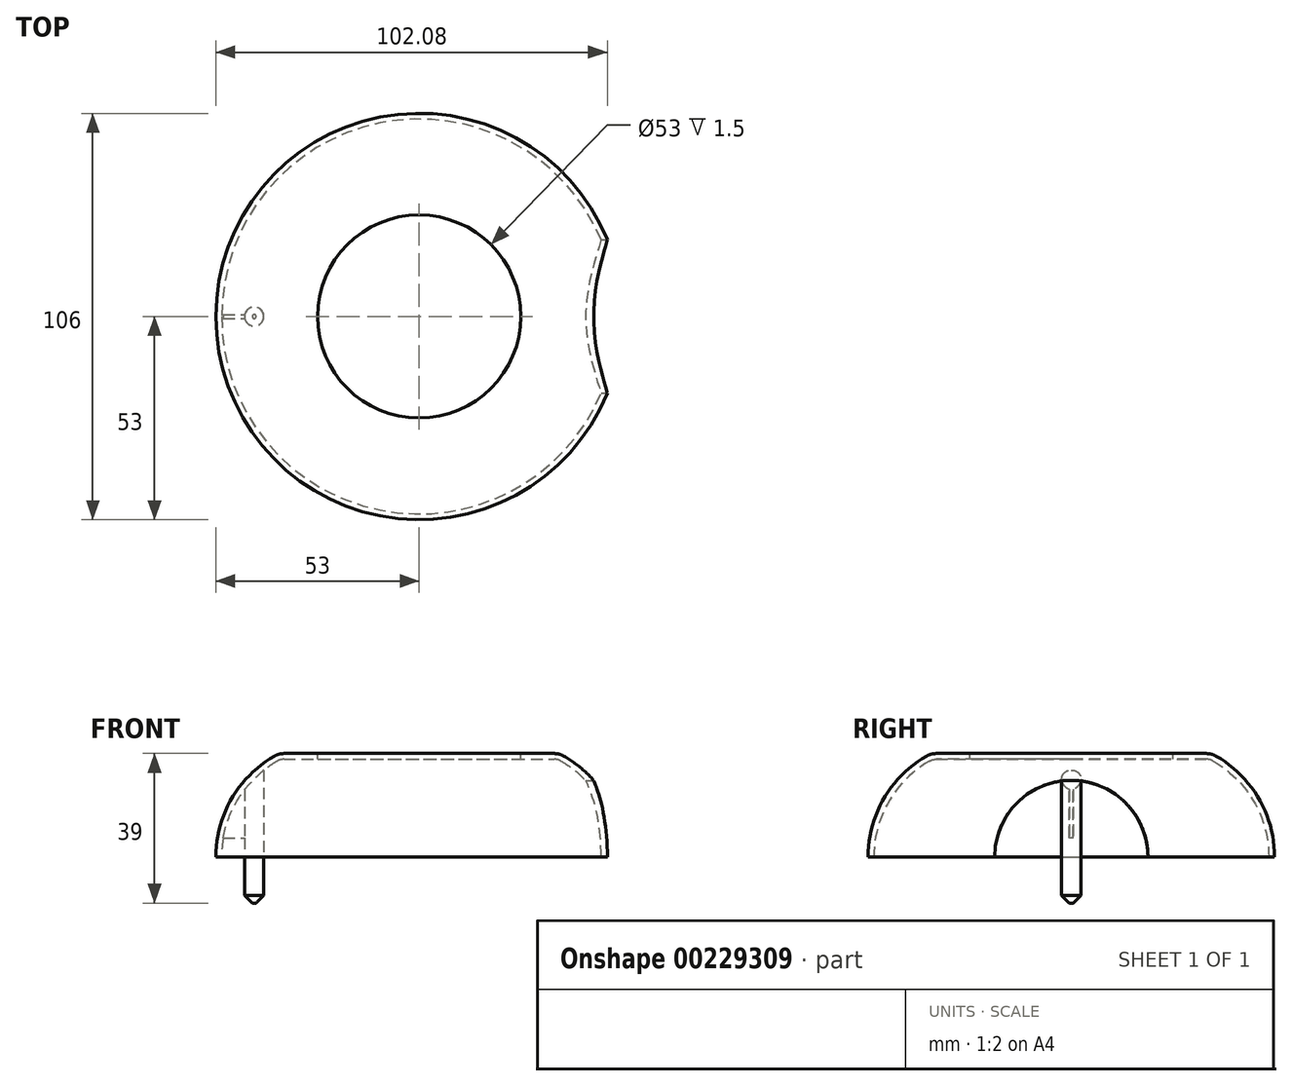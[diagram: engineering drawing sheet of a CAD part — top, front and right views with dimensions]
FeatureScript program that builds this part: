
annotation { "Feature Type Name" : "Feature", "Feature Type Description" : "" }
export const myFeature = defineFeature(function(context is Context, id is Id, definition is map)
    precondition{}
    {
        {
            var Q0;
            Q0=qCreatedBy(makeId("Front.planeOp"),FACE);
            var sketch = newSketch(context, id + "F0", { "sketchPlane" : qUnion([Q0])});
            skLineSegment(sketch, "E0", {"start": v(0, 0) * mm, "end": v(0, 82.4) * mm, "construction": true});
            skLineSegment(sketch, "E1", {"start": v(0, 0) * mm, "end": v(53, 0) * mm, "construction": true});
            skLineSegment(sketch, "E2", {"start": v(0, 27) * mm, "end": v(35.24, 27) * mm});
            skLineSegment(sketch, "E3", {"start": v(53, 0) * mm, "end": v(53, 45.88) * mm, "construction": true});
            skArc(sketch, "E4", {"start": v(53, 0) * mm, "mid": v(48.9, 15.23) * mm, "end": v(37.72, 26.34) * mm});
            skPoint(sketch, "E5.visualSharp", {"position": v(36.5, 27) * mm});
            skArc(sketch, "E5.filletArc", {"start": v(37.72, 26.34) * mm, "mid": v(36.52, 26.83) * mm, "end": v(35.24, 27) * mm});
            skLineSegment(sketch, "E6", {"start": v(0, 27) * mm, "end": v(0, 0) * mm});
            skLineSegment(sketch, "E7", {"start": v(0, 0) * mm, "end": v(53, 0) * mm});
            skSolve(sketch);
        }
        {
            var Q0;
            Q0=makeQuery(id+"F0.imprint","IMPRINT",FACE,{"disambiguationData":[TD([[makeQuery(id+"F0.imprint","IMPRINT",EDGE,{"derivedFrom":sQuery(id+"F0.wireOp",EDGE,"E2")}),-1.0]])]});
            var Q1;
            Q1=sQuery(id+"F0.wireOp",EDGE,"E0");
            revolve(context, id + "F1", {"entities" : qUnion([Q0]), "axis" : qUnion([Q1]), "revolveType" : RevolveType.FULL});
        }
        {
            var Q0;
            Q0=makeQuery(id+"F1.opRevolve","SWEPT_FACE",FACE,{"disambiguationData":[OSD([sQuery(id+"F0.wireOp",EDGE,"E7")])]});
            shell(context, id + "F2", {"entities" : qUnion([Q0]), "thickness" : 1.5 * mm});
        }
        {
            var Q0;
            Q0=makeQuery(id+"F1.opRevolve","SWEPT_FACE",FACE,{"disambiguationData":[OSD([sQuery(id+"F0.wireOp",EDGE,"E2")])]});
            var sketch = newSketch(context, id + "F3", { "sketchPlane" : qUnion([Q0])});
            skCircle(sketch, "E8", {"center": v(0, 0) * mm, "radius": 26.5 * mm});
            skSolve(sketch);
        }
        {
            var Q0;
            Q0=makeQuery(id+"F3.imprint","IMPRINT",FACE,{"disambiguationData":[TD([[makeQuery(id+"F3.imprint","IMPRINT",EDGE,{"derivedFrom":sQuery(id+"F3.wireOp",EDGE,"E8")}),1.0]])]});
            extrude(context, id + "F4", {"entities" : qUnion([Q0]), "operationType" : NewBodyOperationType.REMOVE, "oppositeDirection" : true, "depth" : 25 * mm});
        }
        {
            var Q0;
            Q0=qCreatedBy(makeId("Right.planeOp"),FACE);
            cPlane(context, id + "F5", {"entities" : qUnion([Q0]), "cplaneType" : CPlaneType.OFFSET, "offset" : 55 * mm, "width" : 150 * mm, "height" : 150 * mm});
        }
        {
            var Q0;
            Q0=qCreatedBy(id+"F5.planeOp",FACE);
            var sketch = newSketch(context, id + "F6", { "sketchPlane" : qUnion([Q0])});
            skArc(sketch, "E9", {"start": v(20, 0) * mm, "mid": v(0, 20) * mm, "end": v(-20, 0) * mm});
            skLineSegment(sketch, "E10", {"start": v(-20, 0) * mm, "end": v(20, 0) * mm});
            skLineSegment(sketch, "E11", {"start": v(-38.6, -18.5) * mm, "end": v(-32.6, -27.22) * mm});
            skSolve(sketch);
        }
        {
            var Q0;
            Q0=makeQuery(id+"F6.imprint","IMPRINT",FACE,{"disambiguationData":[TD([[makeQuery(id+"F6.imprint","IMPRINT",EDGE,{"derivedFrom":sQuery(id+"F6.wireOp",EDGE,"E9")}),1.0]])]});
            extrude(context, id + "F7", {"entities" : qUnion([Q0]), "operationType" : NewBodyOperationType.REMOVE, "oppositeDirection" : true, "depth" : 25 * mm});
        }
        {
            var Q0;
            Q0=qCreatedBy(makeId("Top.planeOp"),FACE);
            var sketch = newSketch(context, id + "F8", { "sketchPlane" : qUnion([Q0])});
            skCircle(sketch, "E12", {"center": v(-43, 0) * mm, "radius": 2.5 * mm});
            skPoint(sketch, "E13.0", {"position": v(-53, 0) * mm});
            skLineSegment(sketch, "E14", {"start": v(-53, 0) * mm, "end": v(-53, -27.75) * mm, "construction": true});
            skSolve(sketch);
        }
        {
            var Q0;
            Q0=makeQuery(id+"F8.imprint","IMPRINT",FACE,{"disambiguationData":[TD([[makeQuery(id+"F8.imprint","IMPRINT",EDGE,{"derivedFrom":sQuery(id+"F8.wireOp",EDGE,"E12")}),1.0]])]});
            extrude(context, id + "F9", {"entities" : qUnion([Q0]), "operationType" : NewBodyOperationType.ADD, "endBound" : BoundingType.UP_TO_NEXT, "depth" : 25 * mm});
        }
        {
            var Q0;
            Q0=makeQuery(id+"F9.opExtrude","CAP_FACE",FACE,{"disambiguationData":[OSD([sQuery(id+"F8.wireOp",EDGE,"E12")])],"isStart":true});
            extrude(context, id + "F10", {"entities" : qUnion([Q0]), "operationType" : NewBodyOperationType.ADD, "depth" : 12 * mm});
        }
        {
            var Q0;
            Q0=makeQuery(id+"F10.opExtrude","CAP_EDGE",EDGE,{"disambiguationData":[OSD([sQuery(id+"F8.wireOp",EDGE,"E12")])],"isStart":false});
            chamfer(context, id + "F11", {"entities" : qUnion([Q0]), "width" : 2 * mm, "tangentPropagation" : true});
        }
        {
            var Q0;
            Q0=qCreatedBy(makeId("Top.planeOp"),FACE);
            cPlane(context, id + "F12", {"entities" : qUnion([Q0]), "cplaneType" : CPlaneType.OFFSET, "offset" : 5 * mm, "width" : 150 * mm, "height" : 150 * mm});
        }
        {
            var Q0;
            Q0=qCreatedBy(id+"F12.planeOp",FACE);
            var sketch = newSketch(context, id + "F13", { "sketchPlane" : qUnion([Q0])});
            skPoint(sketch, "E15.0", {"position": v(-51.5, 0) * mm});
            skLineSegment(sketch, "E16", {"start": v(-51.5, 0) * mm, "end": v(-51.5, -8.04) * mm, "construction": true});
            skLineSegment(sketch, "E17", {"start": v(-51.5, 0) * mm, "end": v(-38.92, 0) * mm, "construction": true});
            skLineSegment(sketch, "E18.bottom", {"start": v(-51.85, -0.5) * mm, "end": v(-45.07, -0.5) * mm});
            skLineSegment(sketch, "E18.top", {"start": v(-51.85, 0.5) * mm, "end": v(-45.07, 0.5) * mm});
            skLineSegment(sketch, "E18.left", {"start": v(-51.85, -0.5) * mm, "end": v(-51.85, 0.5) * mm});
            skLineSegment(sketch, "E18.right", {"start": v(-45.07, -0.5) * mm, "end": v(-45.07, 0.5) * mm});
            skSolve(sketch);
        }
        {
            var Q0;
            Q0 = qSketchRegion(id + "F13", true);
            extrude(context, id + "F14", {"entities" : qUnion([Q0]), "operationType" : NewBodyOperationType.ADD, "endBound" : BoundingType.UP_TO_NEXT, "depth" : 25 * mm});
        }
    });
